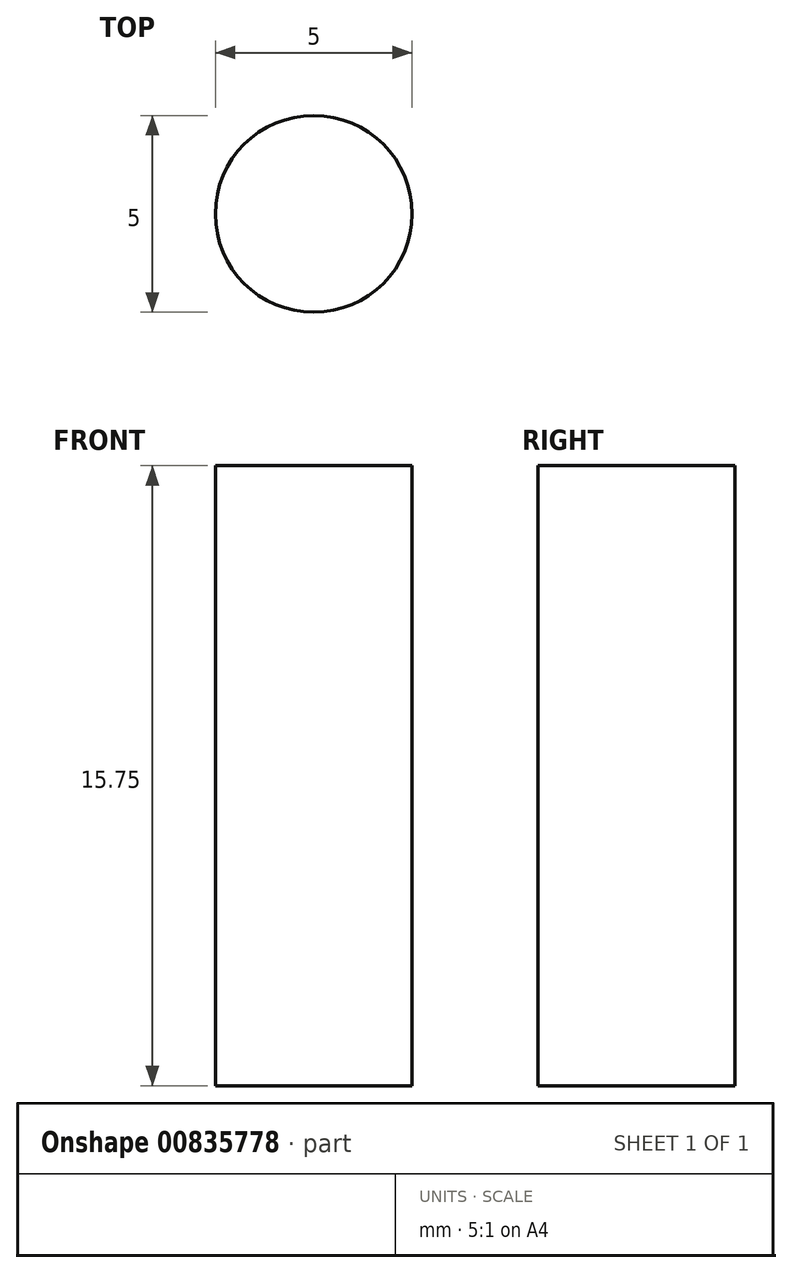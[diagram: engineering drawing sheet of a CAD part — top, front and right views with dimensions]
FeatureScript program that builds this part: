
annotation { "Feature Type Name" : "Feature", "Feature Type Description" : "" }
export const myFeature = defineFeature(function(context is Context, id is Id, definition is map)
    precondition{}
    {
        {
            var Q0;
            Q0=qCreatedBy(makeId("Top.planeOp"),FACE);
            var sketch = newSketch(context, id + "F0", { "sketchPlane" : qUnion([Q0])});
            skLineSegment(sketch, "E0.bottom", {"start": v(-18, 20.15) * mm, "end": v(18, 20.15) * mm, "construction": true});
            skLineSegment(sketch, "E0.top", {"start": v(-18, -20.15) * mm, "end": v(18, -20.15) * mm, "construction": true});
            skLineSegment(sketch, "E0.left", {"start": v(-18, 20.15) * mm, "end": v(-18, -20.15) * mm});
            skLineSegment(sketch, "E0.right", {"start": v(18, 20.15) * mm, "end": v(18, -20.15) * mm});
            skArc(sketch, "E1", {"start": v(18, 20.15) * mm, "mid": v(0, 38.15) * mm, "end": v(-18, 20.15) * mm});
            skArc(sketch, "E2", {"start": v(-18, -20.15) * mm, "mid": v(0, -38.15) * mm, "end": v(18, -20.15) * mm});
            skLineSegment(sketch, "E3", {"start": v(-18, 0) * mm, "end": v(0, 0) * mm, "construction": true});
            skLineSegment(sketch, "E4", {"start": v(0, 0) * mm, "end": v(18, 0) * mm, "construction": true});
            skLineSegment(sketch, "E5", {"start": v(0, 38.15) * mm, "end": v(0, 0) * mm, "construction": true});
            skLineSegment(sketch, "E6", {"start": v(0, 0) * mm, "end": v(0, -38.15) * mm, "construction": true});
            skSolve(sketch);
        }
        {
            var Q0;
            Q0 = qSketchRegion(id + "F0", true);
            extrude(context, id + "F1", {"entities" : qUnion([Q0]), "depth" : 15.75 * mm, "offsetDistance" : 25 * mm});
        }
        {
            var Q0;
            Q0=makeQuery(id+"F1.opExtrude","CAP_FACE",FACE,{"disambiguationData":[OSD([sQuery(id+"F0.wireOp",EDGE,"E0.left"),sQuery(id+"F0.wireOp",EDGE,"E0.right"),sQuery(id+"F0.wireOp",EDGE,"E1"),sQuery(id+"F0.wireOp",EDGE,"E2")])],"isStart":false});
            var sketch = newSketch(context, id + "F2", { "sketchPlane" : qUnion([Q0])});
            skCircle(sketch, "E7", {"center": v(0, 29.15) * mm, "radius": 2.5 * mm});
            skCircle(sketch, "E8.MirrorC", {"center": v(0, -29.15) * mm, "radius": 2.5 * mm});
            skSolve(sketch);
        }
        {
            var Q0;
            Q0=makeQuery(id+"F2.imprint","IMPRINT",FACE,{"disambiguationData":[TD([[makeQuery(id+"F2.imprint","IMPRINT",EDGE,{"derivedFrom":sQuery(id+"F2.wireOp",EDGE,"E7")}),1.0]])]});
            var Q1;
            Q1=makeQuery(id+"F2.imprint","IMPRINT",FACE,{"disambiguationData":[TD([[makeQuery(id+"F2.imprint","IMPRINT",EDGE,{"derivedFrom":sQuery(id+"F2.wireOp",EDGE,"E8.MirrorC")}),-1.0]])]});
            var Q2;
            Q2=sQuery(id+"F2.wireOp",EDGE,"E7");
            var Q3;
            Q3=sQuery(id+"F2.wireOp",EDGE,"E8.MirrorC");
            extrude(context, id + "F3", {"entities" : qUnion([Q0, Q1]), "operationType" : NewBodyOperationType.REMOVE, "surfaceEntities" : qUnion([Q2, Q3]), "endBound" : BoundingType.THROUGH_ALL, "oppositeDirection" : true, "depth" : 25 * mm, "offsetDistance" : 25 * mm});
        }
    });
